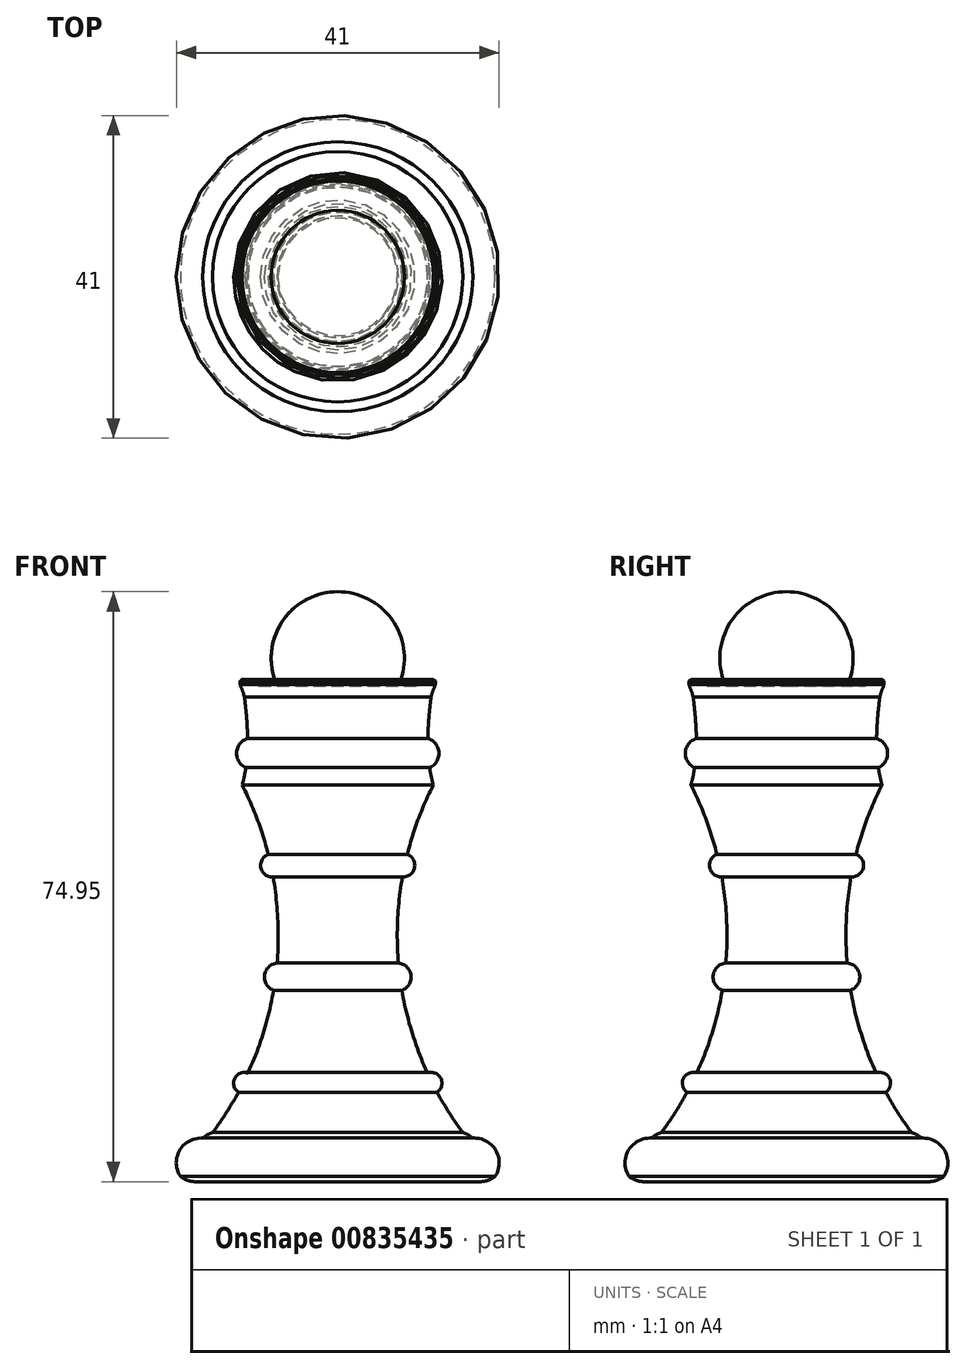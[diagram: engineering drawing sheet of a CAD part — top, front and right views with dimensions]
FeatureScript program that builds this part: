
annotation { "Feature Type Name" : "Feature", "Feature Type Description" : "" }
export const myFeature = defineFeature(function(context is Context, id is Id, definition is map)
    precondition{}
    {
        {
            var Q0;
            Q0=qCreatedBy(makeId("Front.planeOp"),FACE);
            var sketch = newSketch(context, id + "F0", { "sketchPlane" : qUnion([Q0])});
            skLineSegment(sketch, "E0", {"start": v(0, -37.92) * mm, "end": v(0, 18.79) * mm});
            skArc(sketch, "E1", {"start": v(-11.45, 12.13) * mm, "mid": v(-12.85, 10.36) * mm, "end": v(-11.68, 8.42) * mm});
            skFitSpline(sketch, "E2.trimOffspring", {"points": [v(-25.61, -37.92) * mm, v(-19.46, -8.96) * mm, v(-11.68, 8.42) * mm, v(-14.2, 35.39) * mm, v(-12.94, 57.3) * mm, v(-15.84, 63.8) * mm], "startDerivative": vector(16.77, 129.7) * mm, "endDerivative": vector(-31.89, 45.75) * mm});
            skLineSegment(sketch, "E3", {"start": v(-18.05, -44.17) * mm, "end": v(0, -44.17) * mm});
            skLineSegment(sketch, "E4", {"start": v(0, -44.17) * mm, "end": v(0, -37.92) * mm});
            skPoint(sketch, "E5.orphan", {"position": v(-21.75, 63.8) * mm});
            skPoint(sketch, "E6.start.orphan", {"position": v(-18.85, 54.11) * mm});
            skLineSegment(sketch, "E7", {"start": v(-9.95, 18.79) * mm, "end": v(0, 18.79) * mm});
            skPoint(sketch, "E8.start.orphan", {"position": v(-14.2, 38.6) * mm});
            skPoint(sketch, "E9.end.orphan", {"position": v(0, 63.8) * mm});
            skPoint(sketch, "E9.start.orphan", {"position": v(0, 69.76) * mm});
            skPoint(sketch, "E10.end.orphan", {"position": v(-15.84, 69.76) * mm});
            skPoint(sketch, "E11.end.orphan", {"position": v(-18.85, 60.36) * mm});
            skPoint(sketch, "E12.end.orphan", {"position": v(-17.98, 51.2) * mm});
            skPoint(sketch, "E13.orphan", {"position": v(-17.15, -4.34) * mm});
            skPoint(sketch, "E14.orphan", {"position": v(-17.15, -19.25) * mm});
            skLineSegment(sketch, "E15", {"start": v(0, 36.22) * mm, "end": v(0, 11.83) * mm});
            skArc(sketch, "E16", {"start": v(0, 30.78) * mm, "mid": v(-7.12, 26.88) * mm, "end": v(-7.69, 18.79) * mm});
            skArc(sketch, "E17", {"start": v(-11.6, 15.08) * mm, "mid": v(-11.78, 17.07) * mm, "end": v(-12.4, 18.96) * mm});
            skArc(sketch, "E18", {"start": v(-12.45, 19.91) * mm, "mid": v(-12.43, 19.89) * mm, "end": v(-12.4, 19.86) * mm});
            skPoint(sketch, "E19.start.orphan", {"position": v(-14.75, 0) * mm});
            skLineSegment(sketch, "E20", {"start": v(-12.4, 18.96) * mm, "end": v(-12.4, 19.41) * mm});
            skLineSegment(sketch, "E21", {"start": v(-12.4, 19.41) * mm, "end": v(-12.16, 19.63) * mm});
            skPoint(sketch, "E22.start.orphan", {"position": v(-12.93, 19.91) * mm});
            skPoint(sketch, "E23.orphan", {"position": v(-12.4, 19.86) * mm});
            skArc(sketch, "E24.trimOffspring", {"start": v(-12.16, 19.63) * mm, "mid": v(-11.14, 19) * mm, "end": v(-9.95, 18.79) * mm});
            skArc(sketch, "E25", {"start": v(-15.89, -37.92) * mm, "mid": v(-7.71, -16.39) * mm, "end": v(-12.14, 6.22) * mm});
            skArc(sketch, "E26", {"start": v(-15.89, -37.92) * mm, "mid": v(-18.21, -41.05) * mm, "end": v(-15.89, -44.17) * mm});
            skArc(sketch, "E27", {"start": v(-17.15, -38.64) * mm, "mid": v(-20.08, -40.19) * mm, "end": v(-20, -43.5) * mm});
            skArc(sketch, "E28.trimOffspring", {"start": v(-20, -43.5) * mm, "mid": v(-19.08, -44) * mm, "end": v(-18.05, -44.17) * mm});
            skPoint(sketch, "E29.start.orphan", {"position": v(-18.05, -37.92) * mm});
            skPoint(sketch, "E30.start.orphan", {"position": v(-10.49, 0) * mm});
            skArc(sketch, "E31", {"start": v(-8.83, -2.6) * mm, "mid": v(-9.76, -4.3) * mm, "end": v(-8.21, -5.46) * mm});
            skArc(sketch, "E32", {"start": v(-7.71, -16.39) * mm, "mid": v(-9.3, -17.95) * mm, "end": v(-8.15, -19.86) * mm});
            skArc(sketch, "E33", {"start": v(-11.4, -30.38) * mm, "mid": v(-13.09, -31.05) * mm, "end": v(-12.62, -32.8) * mm});
            skSolve(sketch);
        }
        {
            var Q0;
            Q0=qSketchRegion(id+"F0",true);
            var Q1;
            Q1=sQuery(id+"F0.wireOp",EDGE,"E0");
            revolve(context, id + "F1", {"surfaceOperationType" : NewSurfaceOperationType.NEW, "entities" : qUnion([Q0]), "axis" : qUnion([Q1]), "revolveType" : RevolveType.FULL});
        }
    });
